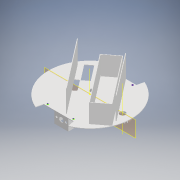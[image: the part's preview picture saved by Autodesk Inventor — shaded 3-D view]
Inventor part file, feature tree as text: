
AUTODESK INVENTOR PART (.ipt)
format: ipt  version: 2020 (Build 240168000, 168)  size: 548,352 bytes
history: native  units: mm
features: sketch x22, extrude x17, reference x13, other x4, fillet x3, projected_geometry x2, plane x1, mirror x1, revolve x1, pattern_circular x1
ambient origin geometry x8: Origin, YZ Plane, XZ Plane, XY Plane, X Axis, Y Axis, Z Axis, Center Point
bodies: Solid1 (feature_tree)
feature tree (65):
  extrude  "Extrusion1"  Depth=1.0mm TaperAngle=0.0deg
  sketch  "Sketch2"  dims[d5=1.0mm d6=0.0mm d29=12.5mm]
  extrude  "Extrusion2"  Depth=12.5mm
  extrude  "Extrusion6"  Depth=1.0mm
  extrude  "Extrusion7"  Depth=8.0mm
  extrude  "Extrusion8"  Depth=1.0mm TaperAngle=0.0deg
  plane  "Work Plane1"
  mirror  "Mirror1"
  extrude  "Extrusion9"  Depth=1.0mm
  extrude  "Extrusion10"  Depth=40.0mm TaperAngle=0.0deg
  extrude  "Extrusion11"  Depth=24.0mm
  extrude  "Extrusion13"  Depth=34.0mm TaperAngle=0.0deg
  other  "Work Axis1"
  extrude  "Extrusion15"  Depth=4.0mm TaperAngle=0.0deg
  fillet  "Fillet2"  Radius=1.0mm
  extrude  "Extrusion21"  Depth=1.0mm TaperAngle=0.0deg
  extrude  "Extrusion24"  Depth=1.0mm
  extrude  "Extrusion25"  Depth=1.0mm
  sketch  "Sketch30"  dims[d105=2.0mm d106=1.0mm d107=0.0mm]
  sketch  "Sketch31"  dims[d111=1.0mm d112=0.0mm d113=2.0mm d114=1.0mm d115=0.0mm]
  extrude  "Extrusion27"  Depth=40.0mm TaperAngle=0.0deg
  fillet  "Fillet6"  Radius=40.0mm
  extrude  "Extrusion28"  Depth=1.0mm TaperAngle=0.0deg
  extrude  "Extrusion29"  Depth=2.0mm
  fillet  "Fillet7"  Radius=1.0mm
  sketch  "Sketch37"  dims[d125=24.0mm]
  extrude  "Extrusion31"  Depth=2.0mm
  sketch  "Sketch39"  dims[d128=2.0mm d129=0.5mm d130=1.570796mm d131=200.0mm d132=360.0deg d17=0.5mm d18=0.872665mm d19=0.5mm d20=0.872665mm d21=0.872665mm d26=0.5mm d27=0.872665mm d28=0.5mm d108=0.5mm d109=0.872665mm d110=0.5mm]
  other  "Work Axis2"
  revolve  "Revolution1"  [1 undecoded]
  pattern_circular  "Circular Pattern2"  [2 undecoded]
  sketch  "Sketch1"  dims[d0=150.0mm d1=1.0mm d2=0.0mm]
  sketch  "Sketch3"  dims[d30=12.5mm d31=1.0mm]
  sketch  "Sketch8"  dims[d32=25.0mm d33=0.0mm d35=8.0mm]
  sketch  "Sketch9"  dims[d37=3.5mm d38=1.0mm d39=0.0mm]
  sketch  "Sketch10"  dims[d41=1.0mm d42=1.0mm]
  sketch  "Sketch11"  dims[d43=20.6mm d44=40.0mm d45=0.0mm]
  sketch  "Sketch12"  dims[d46=106.0mm d47=24.0mm]
  projected_geometry  "Projected Loop4"
  sketch  "Sketch13"  dims[d48=1.0mm d53=34.0mm d54=0.0mm]
  projected_geometry  "Projected Loop5"
  sketch  "Sketch15"  dims[d55=4.0mm d56=0.0mm d57=4.0mm d58=0.0mm d62=1.0mm d63=0.0mm]
  reference  "Reference1"
  reference  "Reference2"
  reference  "Reference3"
  reference  "Reference4"
  reference  "Reference5"
  sketch  "Sketch17"  dims[d71=14.0mm d72=1.0mm d73=0.0mm]
  sketch  "Sketch25"  dims[d85=5.0mm d91=1.0mm]
  sketch  "Sketch28"  dims[d92=40.0mm d93=0.0mm d100=1.0mm]
  sketch  "Sketch29"  dims[d101=1.0mm d102=40.0mm d103=0.0mm d104=40.0mm]
  sketch  "Sketch33"  dims[d116=1.0mm d117=0.0mm d118=2.0mm]
  reference  "Reference12"
  reference  "Reference13"
  reference  "Reference14"
  sketch  "Sketch34"  dims[d122=22.0mm d123=24.0mm]
  reference  "Reference15"
  reference  "Reference16"
  reference  "Reference17"
  reference  "Reference18"
  reference  "Reference19"
  sketch  "Sketch35"  dims[d124=22.0mm]
  sketch  "Sketch38"  dims[d126=6.0mm d127=0.0mm]
  other  "Assembly_for_print.iam"
  other  "DropMechanism_v.2.0:1"
note: 3 required parameter values undecoded (feature->parameter linkage not recoverable at this tier; creation-order binding heuristic only, values carry confidence <= 0.55)